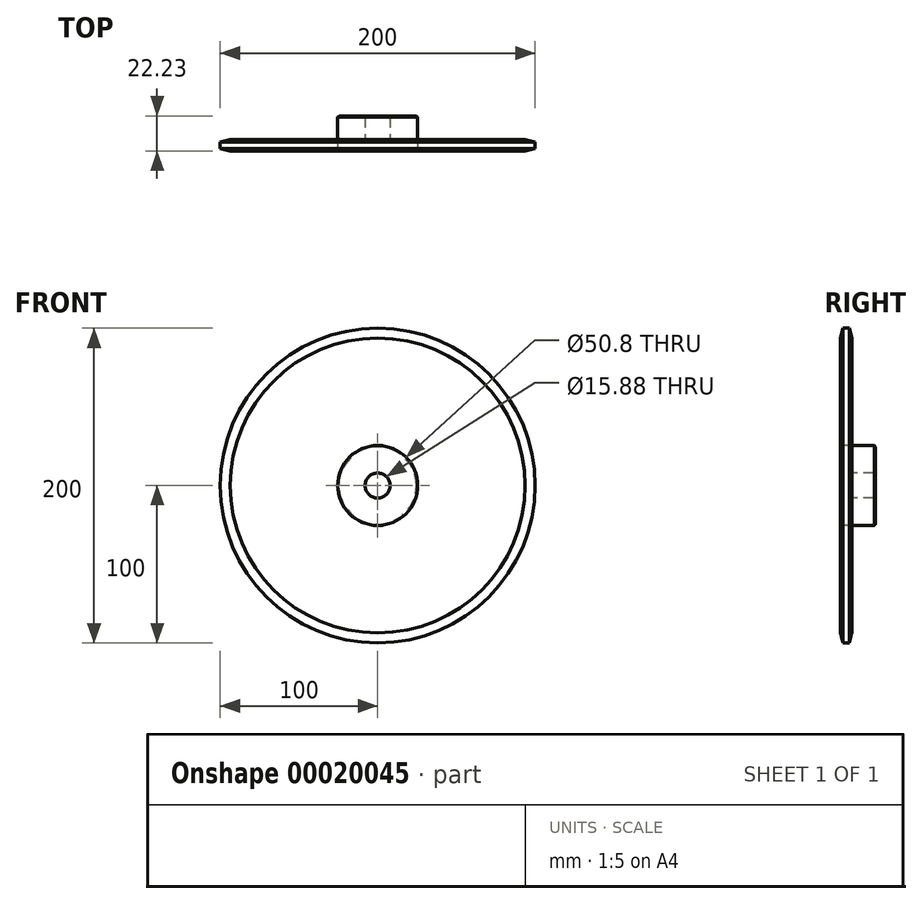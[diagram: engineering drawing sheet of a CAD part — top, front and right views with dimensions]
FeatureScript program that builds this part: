
annotation { "Feature Type Name" : "Feature", "Feature Type Description" : "" }
export const myFeature = defineFeature(function(context is Context, id is Id, definition is map)
    precondition{}
    {
        {
            var Q0;
            Q0=qCreatedBy(makeId("Right.planeOp"),FACE);
            var sketch = newSketch(context, id + "F0", { "sketchPlane" : qUnion([Q0])});
            skLineSegment(sketch, "E0", {"start": v(0, 0) * mm, "end": v(32.17, 0) * mm, "construction": true});
            skLineSegment(sketch, "E1.bottom", {"start": v(0, 7.94) * mm, "end": v(7.21, 7.94) * mm});
            skLineSegment(sketch, "E1.top", {"start": v(0, 100) * mm, "end": v(7.21, 100) * mm});
            skLineSegment(sketch, "E1.left", {"start": v(0, 7.94) * mm, "end": v(0, 100) * mm});
            skLineSegment(sketch, "E1.right", {"start": v(7.21, 7.94) * mm, "end": v(7.21, 100) * mm});
            skLineSegment(sketch, "E2.bottom", {"start": v(0, 7.94) * mm, "end": v(22.23, 7.94) * mm});
            skLineSegment(sketch, "E2.top", {"start": v(0, 25.4) * mm, "end": v(22.23, 25.4) * mm});
            skLineSegment(sketch, "E2.left", {"start": v(0, 7.94) * mm, "end": v(0, 25.4) * mm});
            skLineSegment(sketch, "E2.right", {"start": v(22.23, 7.94) * mm, "end": v(22.23, 25.4) * mm});
            skLineSegment(sketch, "E3.MirrorCS", {"start": v(0, -7.94) * mm, "end": v(0, -25.4) * mm});
            skLineSegment(sketch, "E4.MirrorCS", {"start": v(0, -7.94) * mm, "end": v(7.21, -7.94) * mm});
            skLineSegment(sketch, "E5.MirrorCS", {"start": v(0, -100) * mm, "end": v(7.21, -100) * mm});
            skLineSegment(sketch, "E6.MirrorCS", {"start": v(0, -7.94) * mm, "end": v(0, -100) * mm});
            skLineSegment(sketch, "E7.MirrorCS", {"start": v(7.21, -7.94) * mm, "end": v(7.21, -100) * mm});
            skLineSegment(sketch, "E8.MirrorCS", {"start": v(0, -7.94) * mm, "end": v(22.23, -7.94) * mm});
            skLineSegment(sketch, "E9.MirrorCS", {"start": v(0, -25.4) * mm, "end": v(22.23, -25.4) * mm});
            skLineSegment(sketch, "E10.MirrorCS", {"start": v(22.23, -7.94) * mm, "end": v(22.23, -25.4) * mm});
            skSolve(sketch);
        }
        {
            var Q0;
            {var subQ0=sQuery(id+"F0.wireOp",EDGE,"E2.left");Q0=makeQuery(id+"F0.imprint","IMPRINT",FACE,{"disambiguationData":[TD([[makeQuery(id+"F0.imprint","IMPRINT",EDGE,{"derivedFrom":subQ0}),-1.0]])]});}
            var Q1;
            {var subQ4=sQuery(id+"F0.wireOp",EDGE,"E1.top");Q1=makeQuery(id+"F0.imprint","IMPRINT",FACE,{"disambiguationData":[TD([[makeQuery(id+"F0.imprint","IMPRINT",EDGE,{"derivedFrom":subQ4}),-1.0]])]});}
            var Q2;
            {var subQ0=sQuery(id+"F0.wireOp",EDGE,"E2.right");Q2=makeQuery(id+"F0.imprint","IMPRINT",FACE,{"disambiguationData":[TD([[makeQuery(id+"F0.imprint","IMPRINT",EDGE,{"derivedFrom":subQ0}),1.0]])]});}
            var Q3;
            Q3=sQuery(id+"F0.wireOp",EDGE,"E0");
            revolve(context, id + "F1", {"entities" : qUnion([Q0, Q1, Q2]), "axis" : qUnion([Q3]), "revolveType" : RevolveType.FULL});
        }
        {
            var Q0;
            Q0=makeQuery(id+"F1.opRevolve","SWEPT_EDGE",EDGE,{"disambiguationData":[OSD([sQuery(id+"F0.wireOp",EDGE,"E1.right"),sQuery(id+"F0.wireOp",EDGE,"E2.top")])]});
            fillet(context, id + "F2", {"entities" : qUnion([Q0]), "radius" : 1.59 * mm, "tangentPropagation" : true, "allowEdgeOverflow" : false});
        }
        {
            var Q0;
            Q0=makeQuery(id+"F1.opRevolve","SWEPT_EDGE",EDGE,{"disambiguationData":[OSD([sQuery(id+"F0.wireOp",EDGE,"E2.top"),sQuery(id+"F0.wireOp",EDGE,"E2.right")])]});
            chamfer(context, id + "F3", {"entities" : qUnion([Q0]), "width" : 0.8 * mm, "tangentPropagation" : true});
        }
        {
            var Q0;
            Q0=makeQuery(id+"F1.opRevolve","SWEPT_EDGE",EDGE,{"disambiguationData":[OSD([sQuery(id+"F0.wireOp",EDGE,"E1.top"),sQuery(id+"F0.wireOp",EDGE,"E1.left")])]});
            var Q1;
            Q1=makeQuery(id+"F1.opRevolve","SWEPT_EDGE",EDGE,{"disambiguationData":[OSD([sQuery(id+"F0.wireOp",EDGE,"E1.top"),sQuery(id+"F0.wireOp",EDGE,"E1.right")])]});
            chamfer(context, id + "F4", {"entities" : qUnion([Q0, Q1]), "chamferType" : ChamferType.TWO_OFFSETS, "width1" : 6.35 * mm, "oppositeDirection" : false, "width2" : 1.57 * mm, "tangentPropagation" : true});
        }
    });
